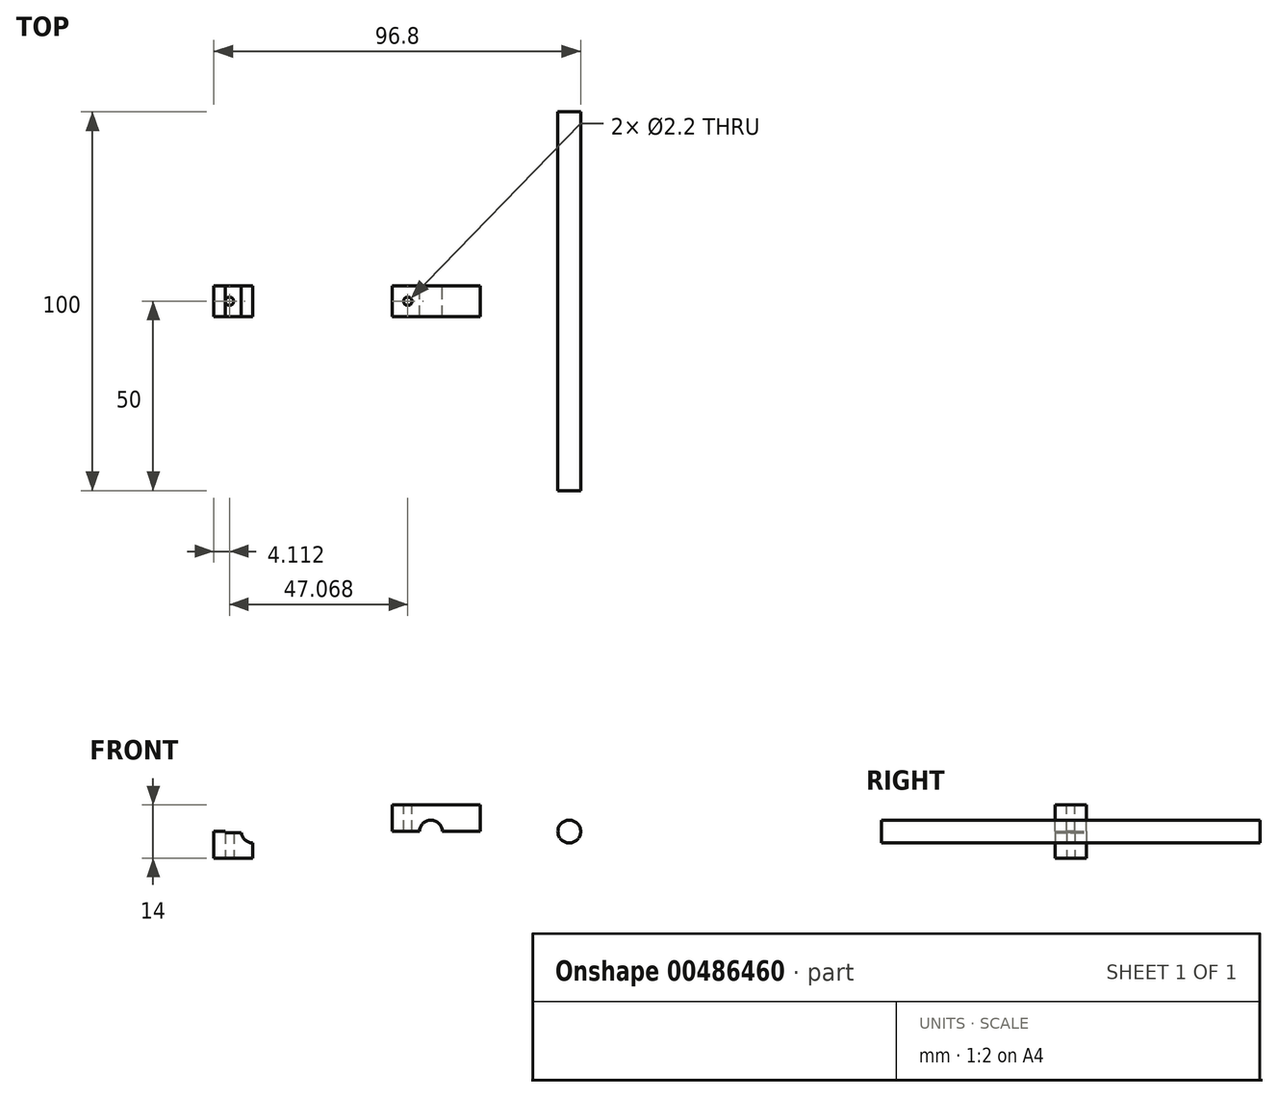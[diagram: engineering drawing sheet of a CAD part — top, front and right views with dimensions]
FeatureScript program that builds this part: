
annotation { "Feature Type Name" : "Feature", "Feature Type Description" : "" }
export const myFeature = defineFeature(function(context is Context, id is Id, definition is map)
    precondition{}
    {
        {
            assignVariable(context, id + "F0", {"name" : "M2_through_hole", "anyValue" : 2.2});
        }
        {
            assignVariable(context, id + "F1", {"name" : "bolt_border_distance", "anyValue" : 3});
        }
        {
            assignVariable(context, id + "F2", {"name" : "top_thickness", "anyValue" : getVariable(context, 'M2_through_hole') + 2 * getVariable(context, 'bolt_border_distance')});
        }
        {
            var Q0;
            Q0=qCreatedBy(makeId("Front.planeOp"),FACE);
            var sketch = newSketch(context, id + "F3", { "sketchPlane" : qUnion([Q0])});
            skCircle(sketch, "E0", {"center": v(0, 0) * mm, "radius": 3 * mm, "construction": true});
            skLineSegment(sketch, "E1.bottom", {"start": v(-10.2, 0) * mm, "end": v(-3, 0) * mm});
            skLineSegment(sketch, "E1.top", {"start": v(-10.2, 7) * mm, "end": v(13, 7) * mm});
            skLineSegment(sketch, "E1.left", {"start": v(-10.2, 0) * mm, "end": v(-10.2, 7) * mm});
            skLineSegment(sketch, "E1.right", {"start": v(13, 0) * mm, "end": v(13, 7) * mm});
            skArc(sketch, "E2", {"start": v(3, 0) * mm, "mid": v(0, 3) * mm, "end": v(-3, 0) * mm});
            skLineSegment(sketch, "E3.trimOffspring", {"start": v(3, 0) * mm, "end": v(13, 0) * mm});
            skSolve(sketch);
        }
        {
            var Q0;
            Q0 = qSketchRegion(id + "F3", true);
            extrude(context, id + "F4", {"entities" : qUnion([Q0]), "depth" : (getVariable(context, 'top_thickness')) * mm, "symmetric" : true});
        }
        {
            var Q0;
            Q0=makeQuery(id+"F4.opExtrude","SWEPT_FACE",FACE,{"disambiguationData":[OSD([sQuery(id+"F3.wireOp",EDGE,"E1.top")])]});
            var sketch = newSketch(context, id + "F5", { "sketchPlane" : qUnion([Q0])});
            skCircle(sketch, "E4", {"center": v(-6.1, 0) * mm, "radius": 1.1 * mm});
            skSolve(sketch);
        }
        {
            var Q0;
            Q0 = qSketchRegion(id + "F5", true);
            extrude(context, id + "F6", {"entities" : qUnion([Q0]), "operationType" : NewBodyOperationType.REMOVE, "endBound" : BoundingType.THROUGH_ALL, "oppositeDirection" : true, "depth" : 25 * mm});
        }
        {
            var Q0;
            Q0=qCreatedBy(makeId("Front.planeOp"),FACE);
            var sketch = newSketch(context, id + "F7", { "sketchPlane" : qUnion([Q0])});
            skArc(sketch, "E5", {"start": v(-47.08, -3) * mm, "mid": v(-44.96, 2.12) * mm, "end": v(-50.08, 0) * mm, "construction": true});
            skLineSegment(sketch, "E6.bottom", {"start": v(-50.08, 0) * mm, "end": v(-47.08, 0) * mm, "construction": true});
            skLineSegment(sketch, "E6.top", {"start": v(-57.28, -7) * mm, "end": v(-47.08, -7) * mm, "construction": true});
            skLineSegment(sketch, "E6.left", {"start": v(-57.28, 0) * mm, "end": v(-57.28, -7) * mm, "construction": true});
            skLineSegment(sketch, "E6.right", {"start": v(-47.08, 0) * mm, "end": v(-47.08, -7) * mm, "construction": true});
            skLineSegment(sketch, "E7", {"start": v(-57.28, 0) * mm, "end": v(-57.28, -7) * mm});
            skLineSegment(sketch, "E8", {"start": v(-57.28, -7) * mm, "end": v(-47.08, -7) * mm});
            skLineSegment(sketch, "E9", {"start": v(-47.08, -7) * mm, "end": v(-47.08, -3) * mm});
            skLineSegment(sketch, "E10", {"start": v(-57.28, 0) * mm, "end": v(-54.28, 0) * mm});
            skLineSegment(sketch, "E11", {"start": v(-54.28, 0) * mm, "end": v(-54.28, -0.3) * mm});
            skCircle(sketch, "E12", {"center": v(-47.08, 0) * mm, "radius": 3 * mm, "construction": true});
            skLineSegment(sketch, "E13", {"start": v(-54.28, -0.3) * mm, "end": v(-50.07, -0.3) * mm});
            skArc(sketch, "E14", {"start": v(-50.07, -0.3) * mm, "mid": v(-49.1, -2.22) * mm, "end": v(-47.08, -3) * mm});
            skSolve(sketch);
        }
        {
            var Q0;
            Q0=makeQuery(id+"F7.imprint","IMPRINT",FACE,{"disambiguationData":[TD([[makeQuery(id+"F7.imprint","IMPRINT",EDGE,{"derivedFrom":sQuery(id+"F7.wireOp",EDGE,"E7")}),1.0]])]});
            extrude(context, id + "F8", {"entities" : qUnion([Q0]), "depth" : (getVariable(context, 'M2_through_hole') + 2 * getVariable(context, 'bolt_border_distance')) * mm, "symmetric" : true});
        }
        {
            var Q0;
            Q0=qCreatedBy(makeId("Front.planeOp"),FACE);
            var sketch = newSketch(context, id + "F9", { "sketchPlane" : qUnion([Q0])});
            skCircle(sketch, "E15", {"center": v(36.52, 0) * mm, "radius": 3 * mm});
            skSolve(sketch);
        }
        {
            var Q0;
            Q0=makeQuery(id+"F9.imprint","IMPRINT",FACE,{"disambiguationData":[TD([[makeQuery(id+"F9.imprint","IMPRINT",EDGE,{"derivedFrom":sQuery(id+"F9.wireOp",EDGE,"E15")}),1.0]])]});
            extrude(context, id + "F10", {"entities" : qUnion([Q0]), "depth" : 100 * mm, "symmetric" : true});
        }
        {
            var Q0;
            Q0=makeQuery(id+"F8.opExtrude","SWEPT_FACE",FACE,{"disambiguationData":[OSD([sQuery(id+"F7.wireOp",EDGE,"E8")])]});
            var sketch = newSketch(context, id + "F11", { "sketchPlane" : qUnion([Q0])});
            skCircle(sketch, "E16", {"center": v(-53.17, 0) * mm, "radius": 1.1 * mm});
            skPoint(sketch, "E17", {"position": v(-47.08, 0) * mm});
            skSolve(sketch);
        }
        {
            var Q0;
            Q0=makeQuery(id+"F11.imprint","IMPRINT",FACE,{"disambiguationData":[TD([[makeQuery(id+"F11.imprint","IMPRINT",EDGE,{"derivedFrom":sQuery(id+"F11.wireOp",EDGE,"E16")}),1.0]])]});
            extrude(context, id + "F12", {"entities" : qUnion([Q0]), "operationType" : NewBodyOperationType.REMOVE, "endBound" : BoundingType.THROUGH_ALL, "oppositeDirection" : true, "depth" : 25 * mm});
        }
    });
